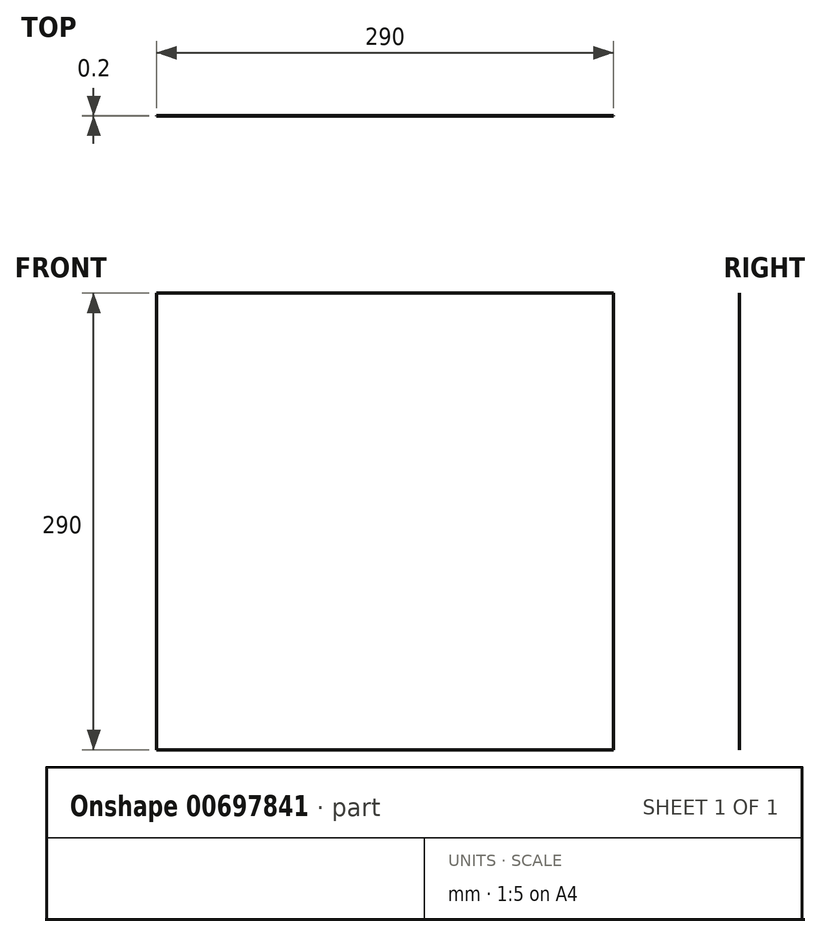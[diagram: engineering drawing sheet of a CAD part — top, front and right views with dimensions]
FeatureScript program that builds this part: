
annotation { "Feature Type Name" : "Feature", "Feature Type Description" : "" }
export const myFeature = defineFeature(function(context is Context, id is Id, definition is map)
    precondition{}
    {
        {
            var Q0;
            Q0=qCreatedBy(makeId("Front.planeOp"),FACE);
            var sketch = newSketch(context, id + "F0", { "sketchPlane" : qUnion([Q0])});
            skLineSegment(sketch, "E0.bottom", {"start": v(-134.78, 139.4) * mm, "end": v(155.22, 139.4) * mm});
            skLineSegment(sketch, "E0.top", {"start": v(-134.78, -150.6) * mm, "end": v(155.22, -150.6) * mm});
            skLineSegment(sketch, "E0.left", {"start": v(-134.78, 139.4) * mm, "end": v(-134.78, -150.6) * mm});
            skLineSegment(sketch, "E0.right", {"start": v(155.22, 139.4) * mm, "end": v(155.22, -150.6) * mm});
            skSolve(sketch);
        }
        {
            var Q0;
            Q0=makeQuery(id+"F0.imprint","IMPRINT",FACE,{"disambiguationData":[TD([[makeQuery(id+"F0.imprint","IMPRINT",EDGE,{"derivedFrom":sQuery(id+"F0.wireOp",EDGE,"E0.bottom")}),-1.0]])]});
            extrude(context, id + "F1", {"entities" : qUnion([Q0]), "depth" : 0.2 * mm, "offsetDistance" : 25 * mm});
        }
    });
